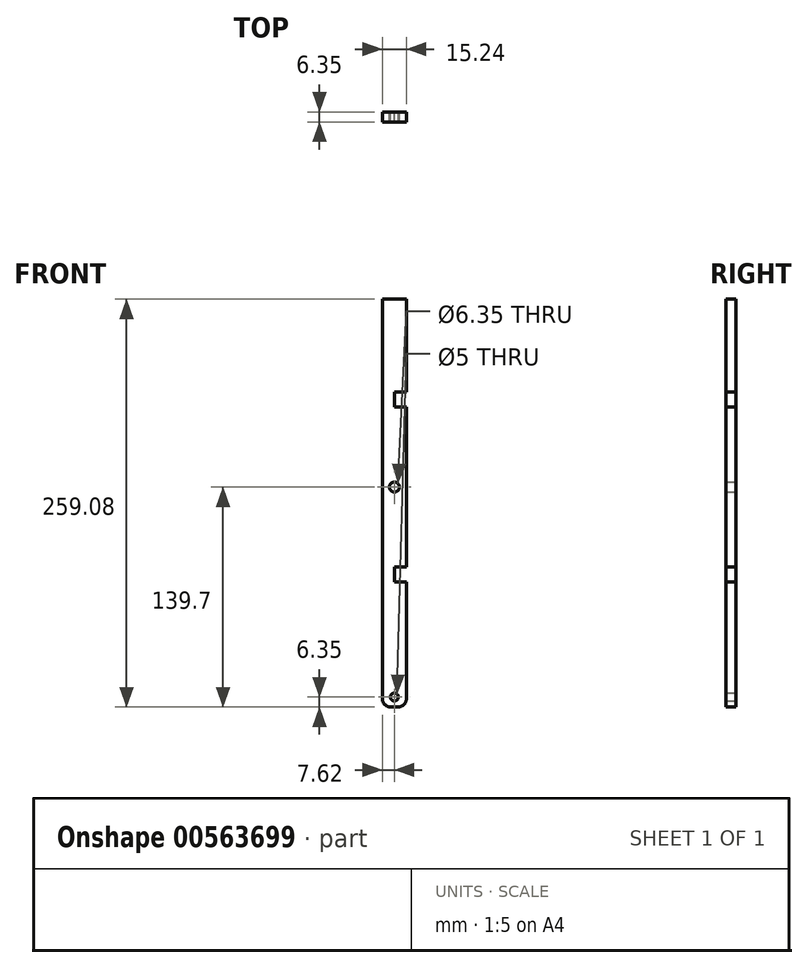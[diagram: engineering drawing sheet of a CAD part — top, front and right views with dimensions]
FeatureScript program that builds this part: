
annotation { "Feature Type Name" : "Feature", "Feature Type Description" : "" }
export const myFeature = defineFeature(function(context is Context, id is Id, definition is map)
    precondition{}
    {
        {
            var Q0;
            Q0=qCreatedBy(makeId("Front.planeOp"),FACE);
            var sketch = newSketch(context, id + "F0", { "sketchPlane" : qUnion([Q0])});
            skLineSegment(sketch, "E0.bottom", {"start": v(0, 0) * mm, "end": v(15.24, 0) * mm});
            skLineSegment(sketch, "E0.top", {"start": v(0, 259.08) * mm, "end": v(15.24, 259.08) * mm});
            skLineSegment(sketch, "E0.left", {"start": v(0, 0) * mm, "end": v(0, 259.08) * mm});
            skLineSegment(sketch, "E0.right", {"start": v(15.24, 0) * mm, "end": v(15.24, 79.38) * mm});
            skCircle(sketch, "E1", {"center": v(7.62, 139.7) * mm, "radius": 3.18 * mm});
            skCircle(sketch, "E2", {"center": v(7.62, 6.35) * mm, "radius": 2.5 * mm});
            skLineSegment(sketch, "E3.bottom", {"start": v(15.24, 200.03) * mm, "end": v(7.62, 200.03) * mm});
            skLineSegment(sketch, "E3.top", {"start": v(15.24, 190.5) * mm, "end": v(7.62, 190.5) * mm});
            skLineSegment(sketch, "E3.right", {"start": v(7.62, 200.03) * mm, "end": v(7.62, 190.5) * mm});
            skLineSegment(sketch, "E4", {"start": v(7.62, 139.7) * mm, "end": v(32.07, 139.7) * mm});
            skLineSegment(sketch, "E5.trimOffspring", {"start": v(15.24, 200.03) * mm, "end": v(15.24, 259.08) * mm});
            skLineSegment(sketch, "E6.MirrorCS", {"start": v(7.62, 79.38) * mm, "end": v(7.62, 88.9) * mm});
            skLineSegment(sketch, "E7.MirrorCS", {"start": v(15.24, 88.9) * mm, "end": v(7.62, 88.9) * mm});
            skLineSegment(sketch, "E8.MirrorCS", {"start": v(15.24, 79.38) * mm, "end": v(7.62, 79.38) * mm});
            skLineSegment(sketch, "E9.trimOffspring", {"start": v(15.24, 88.9) * mm, "end": v(15.24, 190.5) * mm});
            skSolve(sketch);
        }
        {
            var Q0;
            Q0 = qSketchRegion(id + "F0", true);
            extrude(context, id + "F1", {"entities" : qUnion([Q0]), "depth" : 6.35 * mm, "offsetDistance" : 25.4 * mm});
        }
        {
            var Q0;
            Q0=makeQuery(id+"F1.opExtrude","SWEPT_EDGE",EDGE,{"disambiguationData":[OSD([sQuery(id+"F0.wireOp",EDGE,"E0.bottom"),sQuery(id+"F0.wireOp",EDGE,"E0.right")])]});
            var Q1;
            Q1=makeQuery(id+"F1.opExtrude","SWEPT_EDGE",EDGE,{"disambiguationData":[OSD([sQuery(id+"F0.wireOp",EDGE,"E0.bottom"),sQuery(id+"F0.wireOp",EDGE,"E0.left")])]});
            fillet(context, id + "F2", {"entities" : qUnion([Q0, Q1]), "radius" : 5.08 * mm, "tangentPropagation" : true, "allowEdgeOverflow" : false});
        }
    });
